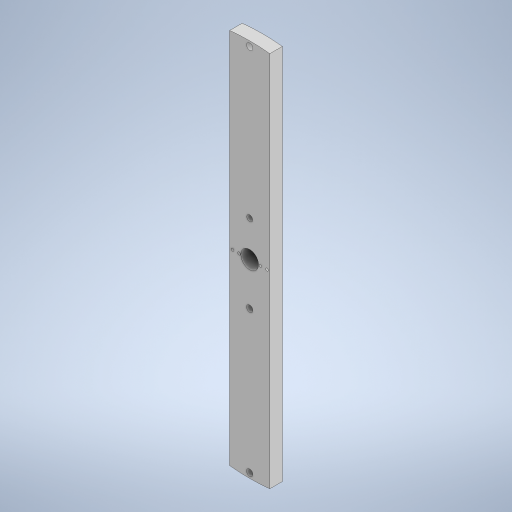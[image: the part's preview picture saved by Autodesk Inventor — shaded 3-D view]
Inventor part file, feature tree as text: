
AUTODESK INVENTOR PART (.ipt)
format: ipt  version: 2023 (Build 270158000, 158)  size: 259,072 bytes
history: native  units: mm
features: other x1, extrude x1, sketch x1
ambient origin geometry x8: Origin, YZ Plane, XZ Plane, XY Plane, X Axis, Y Axis, Z Axis, Center Point
bodies: Body1 (feature_tree)
feature tree (3):
  other  "솔리드1"
  extrude  "돌출1"  Depth=16.0mm
  sketch  "스케치1"
